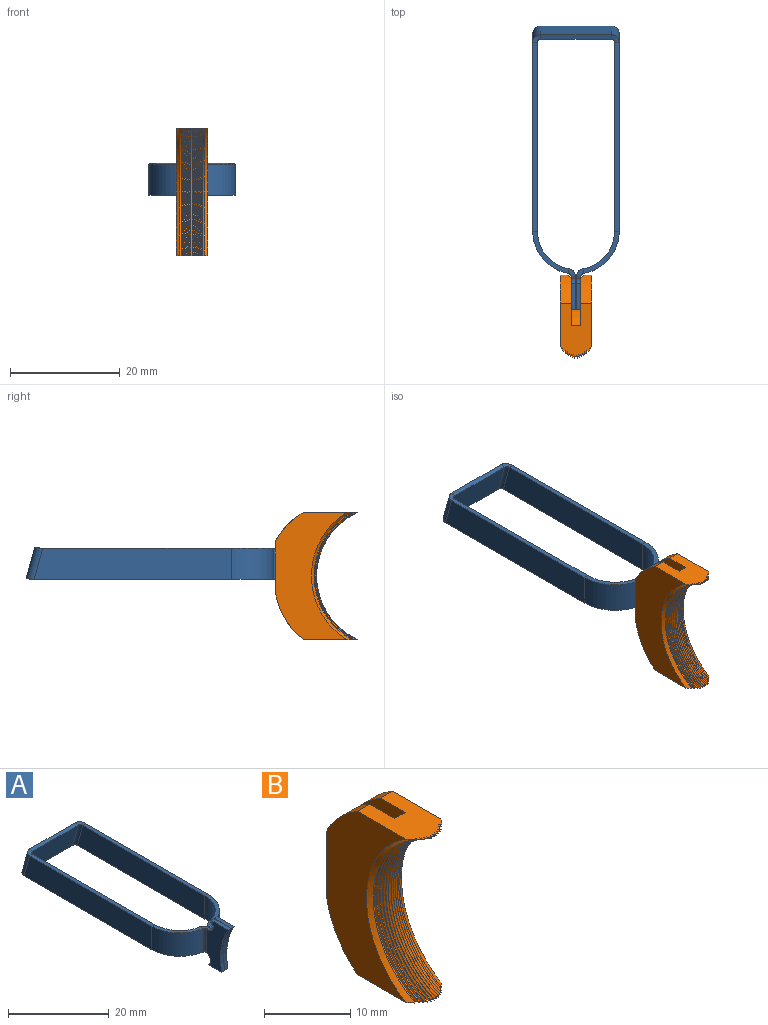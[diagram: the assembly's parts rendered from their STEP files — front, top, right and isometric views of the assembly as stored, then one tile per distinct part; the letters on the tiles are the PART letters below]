
ASSEMBLY  parts=2 mates=1
PART A: 54 faces, bbox 15.8x51.8x11.2 mm
  f0: plane 34.37x0.84mm, normal (0,0,1), area 28.8mm2, adj f2,f3,f4,f51
  f1: plane 35.95x0.84mm, normal (0,0,-1), area 30.1mm2, adj f2,f3,f5,f50
  f2: plane 35.95x5.69mm, normal (-1,0,0), area 200mm2, adj f0,f1,f6,f52
  f3: plane 35.95x5.69mm, normal (1,0,0), area 200mm2, adj f0,f1,f7,f53
  f4: plane 7.73x6.63mm, normal (0,0,1), area 8.7mm2, adj f0,f6,f7,f17
  f5: plane 7.73x6.63mm, normal (0,0,-1), area 8.7mm2, adj f1,f6,f7,f18
  f6: cylinder r=7.85mm len=7.73mm, axis (0,0,-1), area 62.4mm2, adj f2,f4,f5,f20
  f7: cylinder r=7.01mm len=6.9mm, axis (0,0,-1), area 55.7mm2, adj f3,f4,f5,f19
  f8: plane 0.84x0.05mm, normal (0,1,0), area 0mm2, adj f9,f10,f11,f18
  f9: plane 11.18x6mm, normal (1,0,0), area 42.7mm2, adj f8,f10,f12,f13,f14,f15,f16,f19
  f10: cylinder r=1.52mm len=2.65mm, axis (1,0,0), area 2.8mm2, adj f8,f9,f11,f12
  f11: plane 11.18x6mm, normal (-1,0,0), area 42.7mm2, adj f8,f10,f12,f13,f14,f15,f16,f20
  f12: plane 3.69x0.84mm, normal (0,0,-1), area 3.1mm2, adj f9,f10,f11,f13
  f13: cylinder r=16mm len=11.18mm, axis (1,0,0), area 9.7mm2, adj f9,f11,f12,f14
  f14: plane 4.77x0.84mm, normal (0,0,1), area 4mm2, adj f9,f11,f13,f15
  f15: cylinder r=1.52mm len=2.79mm, axis (1,0,0), area 3.3mm2, adj f9,f11,f14,f16
  f16: plane 0.84x0.39mm, normal (0,0,1), area 0.3mm2, adj f9,f11,f15,f17
  f17: plane 1.45x1.36mm, normal (0,0,1), area 1.2mm2, adj f4,f16,f19,f20
  f18: plane 1.45x1.36mm, normal (0,0,-1), area 1.2mm2, adj f5,f8,f19,f20
  f19: cylinder r=1.47mm len=5.69mm, axis (0,0,1), area 11.7mm2, adj f7,f9,f17,f18
  f20: cylinder r=0.64mm len=5.69mm, axis (0,0,1), area 5mm2, adj f6,f11,f17,f18
  f21: plane 12.83x0.81mm, normal (0,0.27,-0.96), area 10.8mm2, adj f23,f24,f46,f50
  f22: plane 12.83x0.81mm, normal (0,-0.27,0.96), area 10.8mm2, adj f23,f24,f47,f51
  f23: plane 12.83x5.69mm, normal (0,0.96,0.27), area 75.7mm2, adj f21,f22,f48,f52
  f24: plane 12.83x5.69mm, normal (0,-0.96,-0.27), area 75.7mm2, adj f21,f22,f49,f53
  f25: plane 34.37x0.84mm, normal (0,0,1), area 28.8mm2, adj f27,f28,f29,f47
  f26: plane 35.95x0.84mm, normal (0,0,-1), area 30.1mm2, adj f27,f28,f30,f46
  f27: plane 35.95x5.69mm, normal (1,0,0), area 200mm2, adj f25,f26,f31,f48
  f28: plane 35.95x5.69mm, normal (-1,0,0), area 200mm2, adj f25,f26,f32,f49
  f29: plane 7.73x6.63mm, normal (0,0,1), area 8.7mm2, adj f25,f31,f32,f42
  f30: plane 7.73x6.63mm, normal (0,0,-1), area 8.7mm2, adj f26,f31,f32,f43
  f31: cylinder r=7.85mm len=7.73mm, axis (0,0,-1), area 62.4mm2, adj f27,f29,f30,f45
  f32: cylinder r=7.01mm len=6.9mm, axis (0,0,-1), area 55.7mm2, adj f28,f29,f30,f44
  f33: plane 11.18x6mm, normal (1,0,0), area 42.7mm2, adj f34,f36,f37,f38,f39,f40,f41,f45
  f34: cylinder r=1.52mm len=2.65mm, axis (-1,0,0), area 2.8mm2, adj f33,f35,f40,f41
  f35: plane 11.18x6mm, normal (-1,0,0), area 42.7mm2, adj f34,f36,f37,f38,f39,f40,f41,f44
  f36: plane 0.84x0.39mm, normal (0,0,1), area 0.3mm2, adj f33,f35,f37,f42
  f37: cylinder r=1.52mm len=2.79mm, axis (-1,0,0), area 3.3mm2, adj f33,f35,f36,f38
  f38: plane 4.77x0.84mm, normal (0,0,1), area 4mm2, adj f33,f35,f37,f39
  f39: cylinder r=16mm len=11.18mm, axis (-1,0,0), area 9.7mm2, adj f33,f35,f38,f40
  f40: plane 3.69x0.84mm, normal (0,0,-1), area 3.1mm2, adj f33,f34,f35,f39
  f41: plane 0.84x0.05mm, normal (0,1,0), area 0mm2, adj f33,f34,f35,f43
  f42: plane 1.45x1.36mm, normal (0,0,1), area 1.2mm2, adj f29,f36,f44,f45
  f43: plane 1.45x1.36mm, normal (0,0,-1), area 1.2mm2, adj f30,f41,f44,f45
  f44: cylinder r=1.47mm len=5.69mm, axis (0,0,1), area 11.7mm2, adj f32,f35,f42,f43
  f45: cylinder r=0.64mm len=5.69mm, axis (0,0,1), area 5mm2, adj f31,f33,f42,f43
  f46: bspline ~1.47x1.47mm, area 1.4mm2, adj f21,f26,f48,f49
  f47: bspline ~1.47x1.47mm, area 1.4mm2, adj f22,f25,f48,f49
  f48: cylinder r=1.47mm len=6.25mm, axis (0,0.27,-0.96), area 13.7mm2, adj f23,f27,f46,f47
  f49: cylinder r=0.64mm len=6.03mm, axis (0,0.27,-0.96), area 5.9mm2, adj f24,f28,f46,f47
  f50: bspline ~1.47x1.47mm, area 1.4mm2, adj f1,f21,f52,f53
  f51: bspline ~1.47x1.47mm, area 1.4mm2, adj f0,f22,f52,f53
  f52: cylinder r=1.47mm len=6.25mm, axis (0,0.27,-0.96), area 13.7mm2, adj f2,f23,f50,f51
  f53: cylinder r=0.64mm len=6.03mm, axis (0,0.27,-0.96), area 5.9mm2, adj f3,f24,f50,f51
PART B: 49 faces, bbox 6.9x15.2x28 mm
  f0: cylinder r=13.82mm len=8.8mm, axis (-1,0,0), area 20.3mm2, adj f1,f3,f5,f46,f47
  f1: plane 9.03x1.4mm, normal (0,1,0), area 12.6mm2, adj f0,f2,f3,f47
  f2: cylinder r=13.46mm len=5.39mm, axis (-1,0,0), area 14.9mm2, adj f1,f3,f9,f46,f47
  f3: plane 23.22x13.05mm, normal (1,0,0), area 169.9mm2, adj f0,f1,f2,f5,f9,f42
  f4: plane 23.22x13.05mm, normal (-1,0,0), area 169.9mm2, adj f5,f6,f7,f8,f9,f43
  f5: plane 9.99x5.76mm, normal (0,0,-1), area 45.5mm2, adj f0,f3,f4,f6,f10,f11,f12,f13
  f6: cylinder r=13.82mm len=8.8mm, axis (-1,0,0), area 20.3mm2, adj f4,f5,f7,f44,f48
  f7: plane 9.03x1.4mm, normal (0,1,0), area 12.6mm2, adj f4,f6,f8,f48
  f8: cylinder r=13.46mm len=5.39mm, axis (-1,0,0), area 14.9mm2, adj f4,f7,f9,f44,f48
  f9: plane 9.98x5.76mm, normal (0,0,1), area 45.4mm2, adj f2,f3,f4,f8,f10,f11,f12,f13
  f10: cone r=13.33mm half-angle=20deg, axis (-1,0,0), area 8mm2, adj f5,f9,f11,f42
  f11: cone r=13.07mm half-angle=70deg, axis (1,0,0), area 8mm2, adj f5,f9,f10,f12
  f12: torus R=17.48mm, axis (1,0,0), area 0.5mm2, adj f5,f9,f11,f13
  f13: cone r=13.18mm half-angle=25deg, axis (-1,0,0), area 8mm2, adj f5,f9,f12,f14
  f14: cone r=12.92mm half-angle=65deg, axis (1,0,0), area 8.1mm2, adj f5,f9,f13,f15
  f15: torus R=17.48mm, axis (1,0,0), area 0.5mm2, adj f5,f9,f14,f16
  f16: cone r=13.06mm half-angle=30deg, axis (-1,0,0), area 8.1mm2, adj f5,f9,f15,f17
  f17: cone r=12.82mm half-angle=60deg, axis (1,0,0), area 8.1mm2, adj f5,f9,f16,f18
  f18: torus R=17.48mm, axis (1,0,0), area 0.5mm2, adj f5,f9,f17,f19
  f19: cone r=12.97mm half-angle=35deg, axis (-1,0,0), area 8.1mm2, adj f5,f9,f18,f20
  f20: cone r=12.74mm half-angle=55deg, axis (1,0,0), area 8.2mm2, adj f5,f9,f19,f21
  f21: torus R=17.48mm, axis (1,0,0), area 0.5mm2, adj f5,f9,f20,f22
  f22: cone r=12.92mm half-angle=40deg, axis (-1,0,0), area 8.2mm2, adj f5,f9,f21,f23
  f23: cone r=12.7mm half-angle=50deg, axis (1,0,0), area 8.2mm2, adj f5,f9,f22,f24
  f24: torus R=17.48mm, axis (1,0,0), area 0.5mm2, adj f5,f9,f23,f25
  f25: cone r=12.7mm half-angle=45deg, axis (-1,0,0), area 8.2mm2, adj f5,f9,f24,f26
  f26: cone r=12.9mm half-angle=45deg, axis (1,0,0), area 8.2mm2, adj f5,f9,f25,f27
  f27: torus R=17.48mm, axis (1,0,0), area 0.5mm2, adj f5,f9,f26,f28
  f28: cone r=12.7mm half-angle=50deg, axis (-1,0,0), area 8.2mm2, adj f5,f9,f27,f29
  f29: cone r=12.92mm half-angle=40deg, axis (1,0,0), area 8.2mm2, adj f5,f9,f28,f30
  f30: torus R=17.48mm, axis (1,0,0), area 0.5mm2, adj f5,f9,f29,f31
  f31: cone r=12.74mm half-angle=55deg, axis (-1,0,0), area 8.2mm2, adj f5,f9,f30,f32
  f32: cone r=12.97mm half-angle=35deg, axis (1,0,0), area 8.1mm2, adj f5,f9,f31,f33
  f33: torus R=17.48mm, axis (1,0,0), area 0.5mm2, adj f5,f9,f32,f34
  f34: cone r=12.82mm half-angle=60deg, axis (-1,0,0), area 8.1mm2, adj f5,f9,f33,f35
  f35: cone r=13.06mm half-angle=30deg, axis (1,0,0), area 8.1mm2, adj f5,f9,f34,f36
  f36: torus R=17.48mm, axis (1,0,0), area 0.5mm2, adj f5,f9,f35,f37
  f37: cone r=12.92mm half-angle=65deg, axis (-1,0,0), area 8.1mm2, adj f5,f9,f36,f38
  f38: cone r=13.18mm half-angle=25deg, axis (1,0,0), area 8mm2, adj f5,f9,f37,f39
  f39: torus R=17.48mm, axis (1,0,0), area 0.5mm2, adj f5,f9,f38,f40
  f40: cone r=13.07mm half-angle=70deg, axis (-1,0,0), area 8mm2, adj f5,f9,f39,f41
  f41: cone r=13.33mm half-angle=20deg, axis (1,0,0), area 8mm2, adj f5,f9,f40,f43
  f42: torus R=17.48mm, axis (1,0,0), area 22.3mm2, adj f3,f5,f9,f10
  f43: torus R=17.48mm, axis (1,0,0), area 22.3mm2, adj f4,f5,f9,f41
  f44: plane 23.22x8.59mm, normal (1,0,0), area 100.3mm2, adj f5,f6,f8,f9,f45,f48
  f45: cylinder r=16mm len=23.22mm, axis (1,0,0), area 43.5mm2, adj f5,f9,f44,f46
  f46: plane 23.22x8.59mm, normal (-1,0,0), area 100.3mm2, adj f0,f2,f5,f9,f45,f47
  f47: plane 12.79x0.76mm, normal (-0.71,0.71,0), area 9.9mm2, adj f0,f1,f2,f46
  f48: plane 12.79x0.76mm, normal (0.71,0.71,0), area 9.9mm2, adj f6,f7,f8,f44
PLACE A t=(0,28.3,2.21)mm
PLACE B at identity fixed
MATE fastened B.f10 <-> A.f13  axis (-1,0,0) through (0.84,0,0)mm
